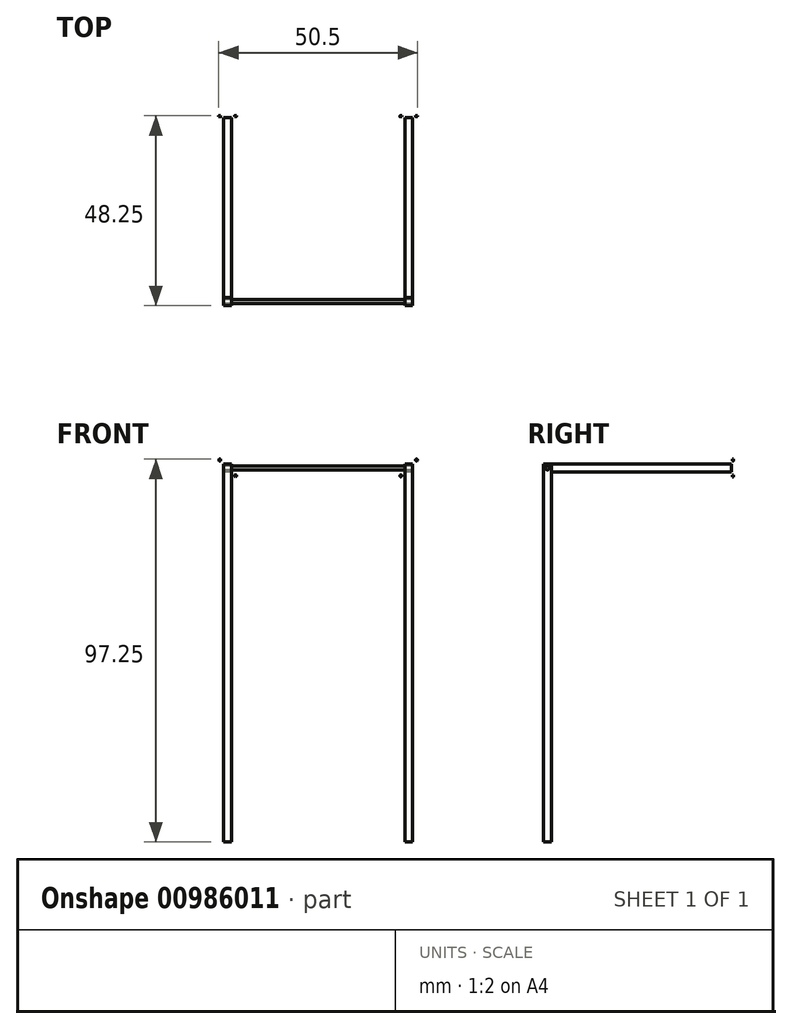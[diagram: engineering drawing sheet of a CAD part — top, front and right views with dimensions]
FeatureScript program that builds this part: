
annotation { "Feature Type Name" : "Feature", "Feature Type Description" : "" }
export const myFeature = defineFeature(function(context is Context, id is Id, definition is map)
    precondition{}
    {
        {
            var Q0;
            Q0=qCreatedBy(makeId("Top.planeOp"),FACE);
            var sketch = newSketch(context, id + "F0", { "sketchPlane" : qUnion([Q0])});
            skLineSegment(sketch, "E0.bottom", {"start": v(-45.92, 41.34) * mm, "end": v(2.08, 41.34) * mm, "construction": true});
            skLineSegment(sketch, "E0.top", {"start": v(-45.92, -6.66) * mm, "end": v(2.08, -6.66) * mm, "construction": true});
            skLineSegment(sketch, "E0.left", {"start": v(-45.92, 41.34) * mm, "end": v(-45.92, -6.66) * mm, "construction": true});
            skLineSegment(sketch, "E0.right", {"start": v(2.08, 41.34) * mm, "end": v(2.08, -6.66) * mm, "construction": true});
            skLineSegment(sketch, "E1", {"start": v(-21.92, 41.34) * mm, "end": v(-21.92, -6.66) * mm, "construction": true});
            skLineSegment(sketch, "E2", {"start": v(-45.92, 17.34) * mm, "end": v(2.08, 17.34) * mm, "construction": true});
            skLineSegment(sketch, "E3.bottom", {"start": v(-45.92, 41.34) * mm, "end": v(-43.92, 41.34) * mm});
            skLineSegment(sketch, "E3.top", {"start": v(-45.92, -6.66) * mm, "end": v(-43.92, -6.66) * mm});
            skLineSegment(sketch, "E3.left", {"start": v(-45.92, 41.34) * mm, "end": v(-45.92, -6.66) * mm});
            skLineSegment(sketch, "E3.right", {"start": v(-43.92, 41.34) * mm, "end": v(-43.92, -6.66) * mm});
            skLineSegment(sketch, "E4.MirrorCS", {"start": v(0.08, 41.34) * mm, "end": v(0.08, -6.66) * mm});
            skLineSegment(sketch, "E5.MirrorCS", {"start": v(2.08, 41.34) * mm, "end": v(0.08, 41.34) * mm});
            skLineSegment(sketch, "E6.MirrorCS", {"start": v(2.08, 41.34) * mm, "end": v(2.08, -6.66) * mm});
            skLineSegment(sketch, "E7.MirrorCS", {"start": v(2.08, -6.66) * mm, "end": v(0.08, -6.66) * mm});
            skLineSegment(sketch, "E8", {"start": v(-45.92, -4.66) * mm, "end": v(-43.92, -4.66) * mm});
            skLineSegment(sketch, "E9.MirrorCS", {"start": v(2.08, -4.66) * mm, "end": v(0.08, -4.66) * mm});
            skLineSegment(sketch, "E10.bottom", {"start": v(-47.92, 41.6) * mm, "end": v(-41.92, 41.6) * mm});
            skLineSegment(sketch, "E10.top", {"start": v(-47.92, 41.34) * mm, "end": v(-41.92, 41.34) * mm});
            skLineSegment(sketch, "E10.left", {"start": v(-47.92, 41.6) * mm, "end": v(-47.92, 41.34) * mm});
            skLineSegment(sketch, "E10.right", {"start": v(-41.92, 41.6) * mm, "end": v(-41.92, 41.34) * mm});
            skLineSegment(sketch, "E11.MirrorCS", {"start": v(4.08, 41.34) * mm, "end": v(-1.92, 41.34) * mm});
            skLineSegment(sketch, "E12.MirrorCS", {"start": v(4.08, 41.6) * mm, "end": v(-1.92, 41.6) * mm});
            skLineSegment(sketch, "E13.MirrorCS", {"start": v(-1.92, 41.6) * mm, "end": v(-1.92, 41.34) * mm});
            skLineSegment(sketch, "E14.MirrorCS", {"start": v(4.08, 41.6) * mm, "end": v(4.08, 41.34) * mm});
            skLineSegment(sketch, "E15.bottom", {"start": v(-47.92, -2.66) * mm, "end": v(-41.92, -2.66) * mm});
            skLineSegment(sketch, "E15.top", {"start": v(-47.92, -8.66) * mm, "end": v(-41.92, -8.66) * mm});
            skLineSegment(sketch, "E15.left", {"start": v(-47.92, -2.66) * mm, "end": v(-47.92, -8.66) * mm});
            skLineSegment(sketch, "E15.right", {"start": v(-41.92, -2.66) * mm, "end": v(-41.92, -8.66) * mm});
            skLineSegment(sketch, "E16.MirrorCS", {"start": v(-1.92, -2.66) * mm, "end": v(-1.92, -8.66) * mm});
            skLineSegment(sketch, "E17.MirrorCS", {"start": v(4.08, -8.66) * mm, "end": v(-1.92, -8.66) * mm});
            skLineSegment(sketch, "E18.MirrorCS", {"start": v(4.08, -2.66) * mm, "end": v(-1.92, -2.66) * mm});
            skLineSegment(sketch, "E19.MirrorCS", {"start": v(4.08, -2.66) * mm, "end": v(4.08, -8.66) * mm});
            skSolve(sketch);
        }
        {
            var Q0;
            {var subQ0=sQuery(id+"F0.wireOp",EDGE,"E3.top");Q0=makeQuery(id+"F0.imprint","IMPRINT",FACE,{"disambiguationData":[TD([[makeQuery(id+"F0.imprint","IMPRINT",EDGE,{"derivedFrom":subQ0}),1.0]])]});}
            var Q1;
            {var subQ0=sQuery(id+"F0.wireOp",EDGE,"E7.MirrorCS");Q1=makeQuery(id+"F0.imprint","IMPRINT",FACE,{"disambiguationData":[TD([[makeQuery(id+"F0.imprint","IMPRINT",EDGE,{"derivedFrom":subQ0}),-1.0]])]});}
            extrude(context, id + "F1", {"entities" : qUnion([Q0, Q1]), "depth" : 96 * mm, "offsetDistance" : 25 * mm});
        }
        {
            var Q0;
            {var subQ0=sQuery(id+"F0.wireOp",EDGE,"E3.left");Q0=makeQuery(id+"F3NXmnak4ZwyZ4x_2.opBoolean","MERGE",FACE,{"derivedFrom":[makeQuery(id+"F1.opExtrude","SWEPT_FACE",FACE,{"disambiguationData":[OSD([subQ0])]}),makeQuery(id+"FC54nujeMIKq3Ik_0.opExtrude","SWEPT_FACE",FACE,{"disambiguationData":[OSD([subQ0])]})]});}
            var sketch = newSketch(context, id + "F2", { "sketchPlane" : qUnion([Q0])});
            skCircle(sketch, "E20", {"center": v(5.66, 95) * mm, "radius": 0.5 * mm});
            skSolve(sketch);
        }
        {
            var Q0;
            Q0=makeQuery(id+"F2.imprint","IMPRINT",FACE,{"disambiguationData":[TD([[makeQuery(id+"F2.imprint","IMPRINT",EDGE,{"derivedFrom":sQuery(id+"F2.wireOp",EDGE,"E20")}),1.0]])]});
            extrude(context, id + "F3", {"entities" : qUnion([Q0]), "oppositeDirection" : true, "depth" : 48 * mm, "offsetDistance" : 25 * mm});
        }
        {
            var Q0;
            Q0=makeQuery(id+"F0.imprint","IMPRINT",FACE,{"disambiguationData":[TD([[makeQuery(id+"F0.imprint","IMPRINT",EDGE,{"derivedFrom":sQuery(id+"F0.wireOp",EDGE,"E12.MirrorCS")}),1.0]])]});
            var Q1;
            Q1=makeQuery(id+"F0.imprint","IMPRINT",FACE,{"disambiguationData":[TD([[makeQuery(id+"F0.imprint","IMPRINT",EDGE,{"derivedFrom":sQuery(id+"F0.wireOp",EDGE,"E10.bottom")}),-1.0]])]});
            extrude(context, id + "F4", {"entities" : qUnion([Q0, Q1]), "depth" : 98 * mm, "offsetDistance" : 25 * mm, "hasSecondDirection" : true, "secondDirectionOppositeDirection" : false, "secondDirectionDepth" : 92 * mm});
        }
        {
            var Q0;
            {var subQ3=sQuery(id+"F0.wireOp",EDGE,"E8");Q0=makeQuery(id+"F0.imprint","IMPRINT",FACE,{"disambiguationData":[TD([[makeQuery(id+"F0.imprint","IMPRINT",EDGE,{"derivedFrom":subQ3}),1.0]])]});}
            var Q1;
            {var subQ3=sQuery(id+"F0.wireOp",EDGE,"E9.MirrorCS");Q1=makeQuery(id+"F0.imprint","IMPRINT",FACE,{"disambiguationData":[TD([[makeQuery(id+"F0.imprint","IMPRINT",EDGE,{"derivedFrom":subQ3}),-1.0]])]});}
            var Q2;
            {var subQ0=sQuery(id+"F0.wireOp",EDGE,"E10.top");var subQ1=sQuery(id+"F0.wireOp",EDGE,"E3.left");var subQ2=makeQuery(id+"F0.imprint","INTERSECT",VERTEX,{"derivedFrom":[subQ1,subQ0]});Q2=makeQuery(id+"F0.imprint","IMPRINT",FACE,{"disambiguationData":[TD([[makeQuery(id+"F0.imprint","IMPRINT",EDGE,{"disambiguationData":[TD([[subQ2,-1.0]])],"derivedFrom":subQ1}),1.0]])]});}
            var Q3;
            {var subQ0=sQuery(id+"F0.wireOp",EDGE,"E11.MirrorCS");var subQ1=sQuery(id+"F0.wireOp",EDGE,"E4.MirrorCS");var subQ2=makeQuery(id+"F0.imprint","INTERSECT",VERTEX,{"derivedFrom":[subQ1,subQ0]});Q3=makeQuery(id+"F0.imprint","IMPRINT",FACE,{"disambiguationData":[TD([[makeQuery(id+"F0.imprint","IMPRINT",EDGE,{"disambiguationData":[TD([[subQ2,-1.0]])],"derivedFrom":subQ1}),1.0]])]});}
            extrude(context, id + "F5", {"entities" : qUnion([Q0, Q1, Q2, Q3]), "depth" : 96 * mm, "offsetDistance" : 25 * mm, "hasSecondDirection" : true, "secondDirectionOppositeDirection" : false, "secondDirectionDepth" : 94 * mm});
        }
        {
            var Q0;
            Q0=makeQuery(id+"F4.opExtrude","SWEPT_FACE",FACE,{"disambiguationData":[OSD([sQuery(id+"F0.wireOp",EDGE,"E10.bottom")])]});
            var sketch = newSketch(context, id + "F6", { "sketchPlane" : qUnion([Q0])});
            skLineSegment(sketch, "E21", {"start": v(44.92, 98) * mm, "end": v(44.92, 92) * mm, "construction": true});
            skLineSegment(sketch, "E22", {"start": v(41.92, 95) * mm, "end": v(47.92, 95) * mm, "construction": true});
            skCircle(sketch, "E23", {"center": v(42.92, 97) * mm, "radius": 0.25 * mm});
            skCircle(sketch, "E24.MirrorC", {"center": v(46.92, 97) * mm, "radius": 0.25 * mm});
            skCircle(sketch, "E25.MirrorC", {"center": v(46.92, 93) * mm, "radius": 0.25 * mm});
            skCircle(sketch, "E26.MirrorC", {"center": v(42.92, 93) * mm, "radius": 0.25 * mm});
            skSolve(sketch);
        }
        {
            var Q0;
            Q0=makeQuery(id+"F6.imprint","IMPRINT",FACE,{"disambiguationData":[TD([[makeQuery(id+"F6.imprint","IMPRINT",EDGE,{"derivedFrom":sQuery(id+"F6.wireOp",EDGE,"E24.MirrorC")}),-1.0]])]});
            var Q1;
            Q1=makeQuery(id+"F6.imprint","IMPRINT",FACE,{"disambiguationData":[TD([[makeQuery(id+"F6.imprint","IMPRINT",EDGE,{"derivedFrom":sQuery(id+"F6.wireOp",EDGE,"E23")}),1.0]])]});
            var Q2;
            Q2=makeQuery(id+"F6.imprint","IMPRINT",FACE,{"disambiguationData":[TD([[makeQuery(id+"F6.imprint","IMPRINT",EDGE,{"derivedFrom":sQuery(id+"F6.wireOp",EDGE,"E26.MirrorC")}),-1.0]])]});
            var Q3;
            Q3=makeQuery(id+"F6.imprint","IMPRINT",FACE,{"disambiguationData":[TD([[makeQuery(id+"F6.imprint","IMPRINT",EDGE,{"derivedFrom":sQuery(id+"F6.wireOp",EDGE,"E25.MirrorC")}),1.0]])]});
            extrude(context, id + "F7", {"entities" : qUnion([Q0, Q1, Q2, Q3]), "operationType" : NewBodyOperationType.REMOVE, "oppositeDirection" : true, "depth" : .5 * mm, "offsetDistance" : 25 * mm});
        }
        {
            var Q0;
            Q0=makeQuery(id+"F4.opExtrude","SWEPT_FACE",FACE,{"disambiguationData":[OSD([sQuery(id+"F0.wireOp",EDGE,"E12.MirrorCS")])]});
            var sketch = newSketch(context, id + "F8", { "sketchPlane" : qUnion([Q0])});
            skLineSegment(sketch, "E27", {"start": v(-1.08, 98) * mm, "end": v(-1.08, 92) * mm, "construction": true});
            skLineSegment(sketch, "E28", {"start": v(-4.08, 95) * mm, "end": v(1.92, 95) * mm, "construction": true});
            skCircle(sketch, "E29", {"center": v(0.92, 97) * mm, "radius": 0.25 * mm});
            skCircle(sketch, "E30.MirrorC", {"center": v(-3.08, 97) * mm, "radius": 0.25 * mm});
            skCircle(sketch, "E31.MirrorC", {"center": v(-3.08, 93) * mm, "radius": 0.25 * mm});
            skCircle(sketch, "E32.MirrorC", {"center": v(0.92, 93) * mm, "radius": 0.25 * mm});
            skSolve(sketch);
        }
        {
            var Q0;
            Q0=makeQuery(id+"F8.imprint","IMPRINT",FACE,{"disambiguationData":[TD([[makeQuery(id+"F8.imprint","IMPRINT",EDGE,{"derivedFrom":sQuery(id+"F8.wireOp",EDGE,"E30.MirrorC")}),-1.0]])]});
            var Q1;
            Q1=makeQuery(id+"F8.imprint","IMPRINT",FACE,{"disambiguationData":[TD([[makeQuery(id+"F8.imprint","IMPRINT",EDGE,{"derivedFrom":sQuery(id+"F8.wireOp",EDGE,"E29")}),1.0]])]});
            var Q2;
            Q2=makeQuery(id+"F8.imprint","IMPRINT",FACE,{"disambiguationData":[TD([[makeQuery(id+"F8.imprint","IMPRINT",EDGE,{"derivedFrom":sQuery(id+"F8.wireOp",EDGE,"E32.MirrorC")}),-1.0]])]});
            var Q3;
            Q3=makeQuery(id+"F8.imprint","IMPRINT",FACE,{"disambiguationData":[TD([[makeQuery(id+"F8.imprint","IMPRINT",EDGE,{"derivedFrom":sQuery(id+"F8.wireOp",EDGE,"E31.MirrorC")}),1.0]])]});
            extrude(context, id + "F9", {"entities" : qUnion([Q0, Q1, Q2, Q3]), "operationType" : NewBodyOperationType.REMOVE, "oppositeDirection" : true, "depth" : .5 * mm, "offsetDistance" : 25 * mm});
        }
    });
